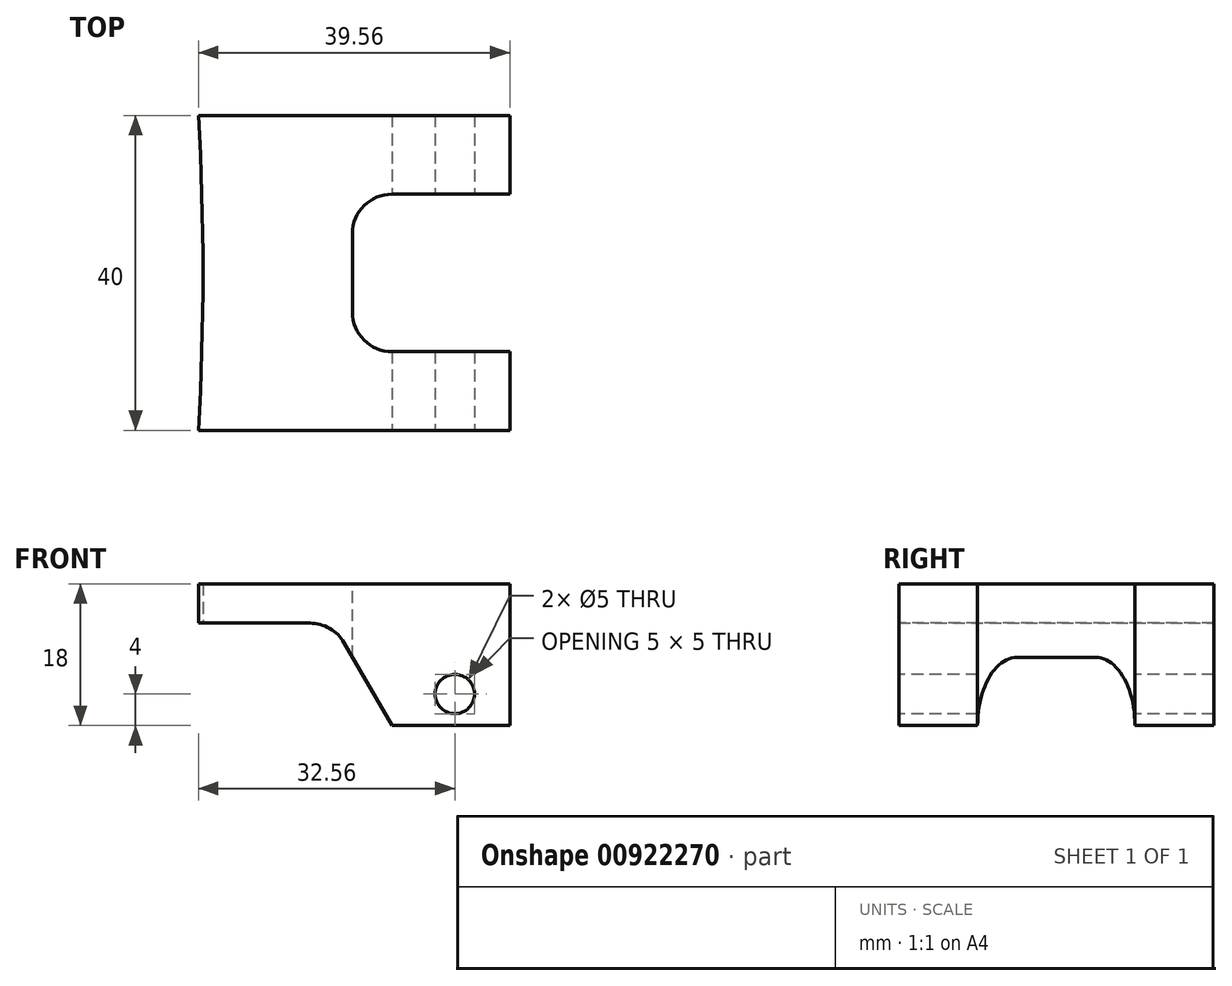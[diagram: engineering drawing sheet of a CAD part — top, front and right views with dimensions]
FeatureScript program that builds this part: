
annotation { "Feature Type Name" : "Feature", "Feature Type Description" : "" }
export const myFeature = defineFeature(function(context is Context, id is Id, definition is map)
    precondition{}
    {
        {
            var Q0;
            Q0=qCreatedBy(makeId("Top.planeOp"),FACE);
            var sketch = newSketch(context, id + "F0", { "sketchPlane" : qUnion([Q0])});
            skCircle(sketch, "E0", {"center": v(-358, 0) * mm, "radius": 358 * mm});
            skLineSegment(sketch, "E1", {"start": v(0, 0) * mm, "end": v(39, 0) * mm, "construction": true});
            skLineSegment(sketch, "E2", {"start": v(-0.56, 20) * mm, "end": v(39, 20) * mm});
            skLineSegment(sketch, "E3", {"start": v(-0.56, -20) * mm, "end": v(39, -20) * mm});
            skLineSegment(sketch, "E4", {"start": v(39, 20) * mm, "end": v(39, -20) * mm});
            skSolve(sketch);
        }
        {
            var Q0;
            {var subQ0=sQuery(id+"F0.wireOp",EDGE,"E2");Q0=makeQuery(id+"F0.imprint","IMPRINT",FACE,{"disambiguationData":[TD([[makeQuery(id+"F0.imprint","IMPRINT",EDGE,{"derivedFrom":subQ0}),-1.0]])]});}
            extrude(context, id + "F1", {"entities" : qUnion([Q0]), "depth" : 9 * mm, "offsetDistance" : 25 * mm, "hasSecondDirection" : true, "secondDirectionOppositeDirection" : true, "secondDirectionDepth" : 9 * mm});
        }
        {
            var Q0;
            Q0=qCreatedBy(makeId("Front.planeOp"),FACE);
            var sketch = newSketch(context, id + "F2", { "sketchPlane" : qUnion([Q0])});
            skLineSegment(sketch, "E5", {"start": v(-7.13, 0) * mm, "end": v(53.36, 0) * mm, "construction": true});
            skLineSegment(sketch, "E6", {"start": v(39, 9) * mm, "end": v(39, -9) * mm});
            skLineSegment(sketch, "E7", {"start": v(39, -9) * mm, "end": v(24, -9) * mm});
            skLineSegment(sketch, "E8", {"start": v(24, -9) * mm, "end": v(17.94, 1.5) * mm});
            skLineSegment(sketch, "E9", {"start": v(13.6, 4) * mm, "end": v(-2.64, 4) * mm});
            skLineSegment(sketch, "E10", {"start": v(-2.64, 4) * mm, "end": v(-2.64, 9) * mm});
            skLineSegment(sketch, "E11", {"start": v(-2.64, 9) * mm, "end": v(39, 9) * mm});
            skPoint(sketch, "E12.visualSharp", {"position": v(16.5, 4) * mm});
            skArc(sketch, "E12.filletArc", {"start": v(17.94, 1.5) * mm, "mid": v(16.1, 3.33) * mm, "end": v(13.6, 4) * mm});
            skLineSegment(sketch, "E13", {"start": v(24, -9) * mm, "end": v(-2.64, -9) * mm});
            skLineSegment(sketch, "E14", {"start": v(-2.64, -9) * mm, "end": v(-2.64, 4) * mm});
            skSolve(sketch);
        }
        {
            var Q0;
            Q0=makeQuery(id+"F2.imprint","IMPRINT",FACE,{"disambiguationData":[TD([[makeQuery(id+"F2.imprint","IMPRINT",EDGE,{"derivedFrom":sQuery(id+"F2.wireOp",EDGE,"E8")}),1.0]])]});
            extrude(context, id + "F3", {"entities" : qUnion([Q0]), "operationType" : NewBodyOperationType.REMOVE, "oppositeDirection" : true, "depth" : 25 * mm, "offsetDistance" : 25 * mm, "hasSecondDirection" : true, "secondDirectionOppositeDirection" : false, "secondDirectionDepth" : 25 * mm});
        }
        {
            var Q0;
            Q0=qCreatedBy(makeId("Top.planeOp"),FACE);
            var sketch = newSketch(context, id + "F4", { "sketchPlane" : qUnion([Q0])});
            skLineSegment(sketch, "E15", {"start": v(19, 0) * mm, "end": v(39, 0) * mm});
            skPoint(sketch, "E16", {"position": v(19, -10) * mm});
            skLineSegment(sketch, "E17.bottom", {"start": v(24, -10) * mm, "end": v(41.6, -10) * mm});
            skLineSegment(sketch, "E17.top", {"start": v(24, 10) * mm, "end": v(41.6, 10) * mm});
            skLineSegment(sketch, "E17.left", {"start": v(19, -5) * mm, "end": v(19, 5) * mm});
            skLineSegment(sketch, "E17.right", {"start": v(41.6, -10) * mm, "end": v(41.6, 10) * mm});
            skArc(sketch, "E18.filletArc", {"start": v(19, -5) * mm, "mid": v(20.46, -8.54) * mm, "end": v(24, -10) * mm});
            skPoint(sketch, "E19.visualSharp", {"position": v(19, 10) * mm});
            skArc(sketch, "E19.filletArc", {"start": v(24, 10) * mm, "mid": v(20.46, 8.54) * mm, "end": v(19, 5) * mm});
            skSolve(sketch);
        }
        {
            var Q0;
            Q0 = qSketchRegion(id + "F4", true);
            extrude(context, id + "F5", {"entities" : qUnion([Q0]), "operationType" : NewBodyOperationType.REMOVE, "oppositeDirection" : true, "depth" : 25 * mm, "offsetDistance" : 25 * mm, "hasSecondDirection" : true, "secondDirectionOppositeDirection" : false, "secondDirectionDepth" : 25 * mm});
        }
        {
            var Q0;
            Q0=qCreatedBy(makeId("Front.planeOp"),FACE);
            var sketch = newSketch(context, id + "F6", { "sketchPlane" : qUnion([Q0])});
            skCircle(sketch, "E20", {"center": v(32, -5) * mm, "radius": 2.5 * mm});
            skSolve(sketch);
        }
        {
            var Q0;
            Q0 = qSketchRegion(id + "F6", true);
            extrude(context, id + "F7", {"entities" : qUnion([Q0]), "operationType" : NewBodyOperationType.REMOVE, "oppositeDirection" : true, "depth" : 25 * mm, "offsetDistance" : 25 * mm, "hasSecondDirection" : true, "secondDirectionOppositeDirection" : false, "secondDirectionDepth" : 25 * mm});
        }
    });
